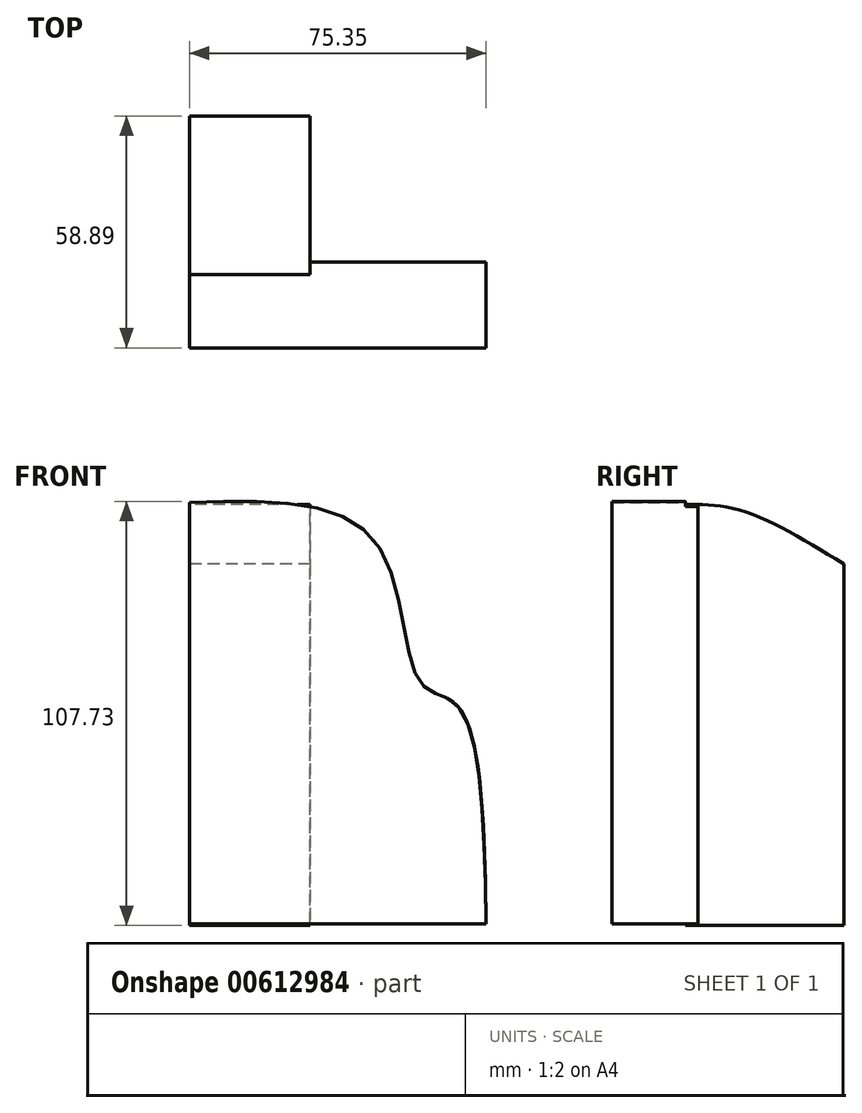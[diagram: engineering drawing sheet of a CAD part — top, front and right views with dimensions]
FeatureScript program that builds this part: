
annotation { "Feature Type Name" : "Feature", "Feature Type Description" : "" }
export const myFeature = defineFeature(function(context is Context, id is Id, definition is map)
    precondition{}
    {
        {
            var Q0;
            Q0=qCreatedBy(makeId("Front.planeOp"),FACE);
            var sketch = newSketch(context, id + "F0", { "sketchPlane" : qUnion([Q0])});
            skFitSpline(sketch, "E0", {"points": [v(0, 31.45) * mm, v(47.2, 21.5) * mm, v(58.46, -14.02) * mm, v(68, -20.08) * mm, v(75.35, -75.52) * mm], "startDerivative": vector(199.39, 7.12) * mm, "endDerivative": vector(4.3, -232.93) * mm});
            skLineSegment(sketch, "E1", {"start": v(75.35, -75.52) * mm, "end": v(0, -75.52) * mm});
            skLineSegment(sketch, "E2", {"start": v(0, -75.52) * mm, "end": v(0, 31.45) * mm});
            skSolve(sketch);
        }
        {
            var Q0;
            Q0=makeQuery(id+"F0.imprint","IMPRINT",FACE,{"disambiguationData":[TD([[makeQuery(id+"F0.imprint","IMPRINT",EDGE,{"derivedFrom":sQuery(id+"F0.wireOp",EDGE,"E0")}),-1.0]])]});
            extrude(context, id + "F1", {"entities" : qUnion([Q0]), "depth" : 18.6 * mm, "offsetDistance" : 25.4 * mm});
        }
        {
            var Q0;
            Q0=qCreatedBy(makeId("Right.planeOp"),FACE);
            var sketch = newSketch(context, id + "F2", { "sketchPlane" : qUnion([Q0])});
            skFitSpline(sketch, "E3", {"points": [v(0, 31.02) * mm, v(14.72, 29.29) * mm, v(40.28, 15.86) * mm], "startDerivative": vector(33.47, -0.2) * mm, "endDerivative": vector(46.37, -28.55) * mm});
            skLineSegment(sketch, "E4", {"start": v(40.28, 15.86) * mm, "end": v(40.28, -75.95) * mm});
            skLineSegment(sketch, "E5", {"start": v(40.28, -75.95) * mm, "end": v(0, -75.95) * mm});
            skLineSegment(sketch, "E6", {"start": v(0, -75.95) * mm, "end": v(0, 31.02) * mm});
            skSolve(sketch);
        }
        {
            var Q0;
            Q0 = qSketchRegion(id + "F2", true);
            var Q1;
            Q1=makeQuery(id+"F2.imprint","IMPRINT",FACE,{"disambiguationData":[TD([[makeQuery(id+"F2.imprint","IMPRINT",EDGE,{"derivedFrom":sQuery(id+"F2.wireOp",EDGE,"E3")}),-1.0]])]});
            extrude(context, id + "F3", {"entities" : qUnion([Q0, Q1]), "operationType" : NewBodyOperationType.ADD, "depth" : 30.63 * mm, "offsetDistance" : 25.4 * mm});
        }
        {
            var Q0;
            {var subQ0=sQuery(id+"F0.wireOp",EDGE,"E0");var subQ2=sQuery(id+"F0.wireOp",EDGE,"E1");Q0=makeQuery(id+"F3.boolean.opBoolean","SPLIT",FACE,{"disambiguationData":[TD([makeQuery(id+"F1.opExtrude","SWEPT_FACE",FACE,{"disambiguationData":[OSD([subQ2])]})])],"derivedFrom":makeQuery(id+"F1.opExtrude","CAP_FACE",FACE,{"disambiguationData":[OSD([subQ0,subQ2,sQuery(id+"F0.wireOp",EDGE,"E2")])],"isStart":true})});}
            extrude(context, id + "F4", {"entities" : qUnion([Q0]), "operationType" : NewBodyOperationType.ADD, "depth" : 3.24 * mm, "offsetDistance" : 25.4 * mm});
        }
    });
